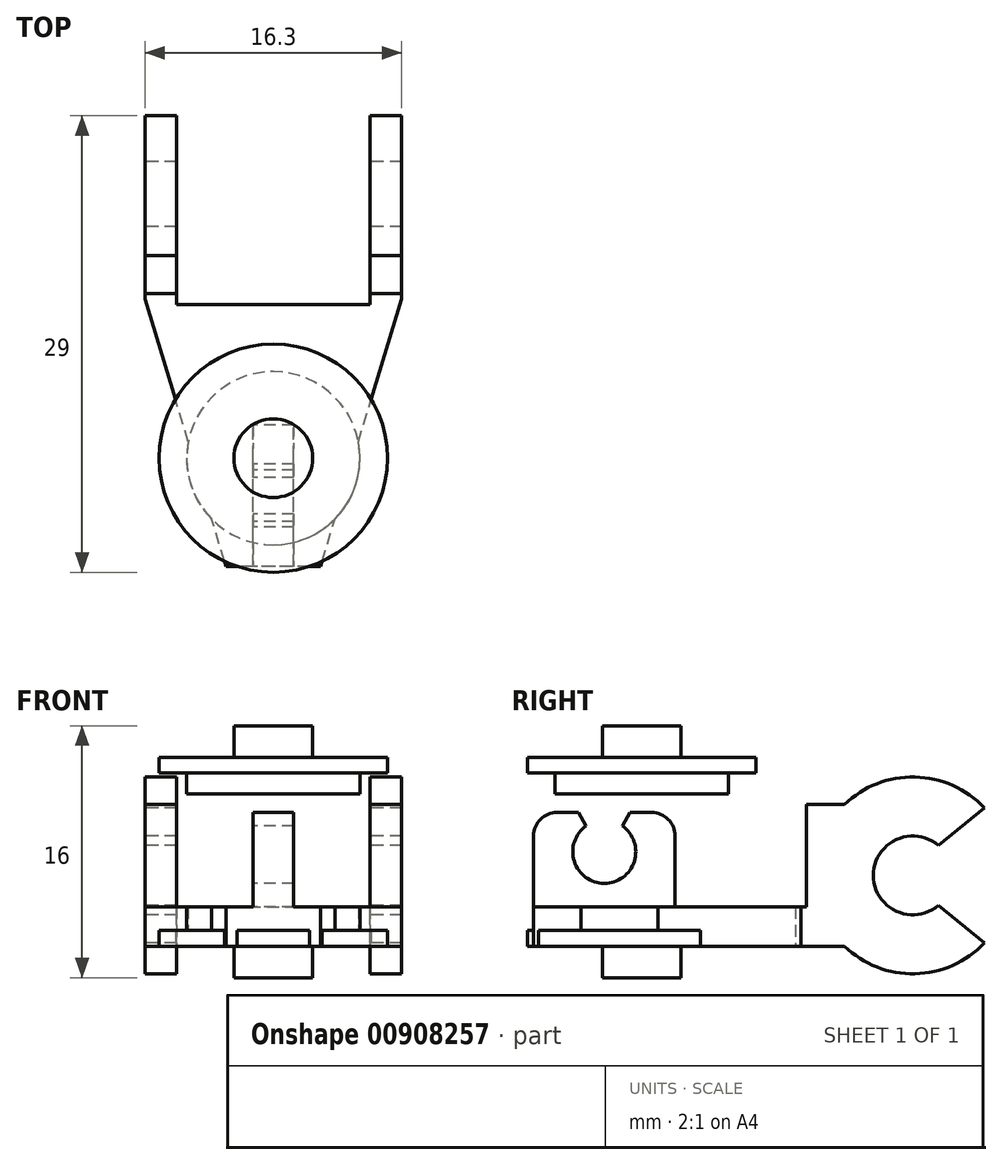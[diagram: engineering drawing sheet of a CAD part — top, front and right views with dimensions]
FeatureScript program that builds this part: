
annotation { "Feature Type Name" : "Feature", "Feature Type Description" : "" }
export const myFeature = defineFeature(function(context is Context, id is Id, definition is map)
    precondition{}
    {
        {
            var Q0;
            Q0=qCreatedBy(makeId("Top.planeOp"),FACE);
            var sketch = newSketch(context, id + "F0", { "sketchPlane" : qUnion([Q0])});
            skCircle(sketch, "E0", {"center": v(0, 0) * mm, "radius": 7.25 * mm});
            skSolve(sketch);
        }
        {
            var Q0;
            Q0 = qSketchRegion(id + "F0", true);
            extrude(context, id + "F1", {"entities" : qUnion([Q0]), "depth" : 1 * mm, "offsetDistance" : 25 * mm});
        }
        {
            var Q0;
            Q0=makeQuery(id+"F1.opExtrude","CAP_FACE",FACE,{"disambiguationData":[OSD([sQuery(id+"F0.wireOp",EDGE,"E0")])],"isStart":false});
            var sketch = newSketch(context, id + "F2", { "sketchPlane" : qUnion([Q0])});
            skCircle(sketch, "E1", {"center": v(0, 0) * mm, "radius": 5.5 * mm});
            skSolve(sketch);
        }
        {
            var Q0;
            Q0 = qSketchRegion(id + "F2", true);
            extrude(context, id + "F3", {"entities" : qUnion([Q0]), "operationType" : NewBodyOperationType.ADD, "depth" : 5 * mm, "offsetDistance" : 25 * mm});
        }
        {
            var Q0;
            Q0=makeQuery(id+"F1.opExtrude","CAP_FACE",FACE,{"disambiguationData":[OSD([sQuery(id+"F0.wireOp",EDGE,"E0")])],"isStart":true});
            var sketch = newSketch(context, id + "F4", { "sketchPlane" : qUnion([Q0])});
            skCircle(sketch, "E2", {"center": v(0, 0) * mm, "radius": 2.5 * mm});
            skSolve(sketch);
        }
        {
            var Q0;
            Q0 = qSketchRegion(id + "F4", true);
            extrude(context, id + "F5", {"entities" : qUnion([Q0]), "operationType" : NewBodyOperationType.ADD, "depth" : 2 * mm, "offsetDistance" : 25 * mm});
        }
        {
            var Q0;
            Q0=makeQuery(id+"F1.opExtrude","SWEPT_BODY",BODY,{"disambiguationData":[OSD([sQuery(id+"F0.wireOp",EDGE,"E0")])]});
            var Q1;
            Q1=makeQuery(id+"F3.opExtrude","CAP_FACE",FACE,{"disambiguationData":[OSD([sQuery(id+"F2.wireOp",EDGE,"E1")])],"isStart":false});
            mirror(context, id + "F6", {"operationType" : NewBodyOperationType.ADD, "entities" : qUnion([Q0]), "mirrorPlane" : qUnion([Q1])});
        }
        {
            var Q0;
            Q0=qCreatedBy(makeId("Top.planeOp"),FACE);
            var sketch = newSketch(context, id + "F7", { "sketchPlane" : qUnion([Q0])});
            skLineSegment(sketch, "E3", {"start": v(0, 13.12) * mm, "end": v(8.15, 13.12) * mm});
            skLineSegment(sketch, "E4", {"start": v(8.15, 13.12) * mm, "end": v(8.15, 10.12) * mm});
            skLineSegment(sketch, "E5", {"start": v(0, -6.88) * mm, "end": v(3, -6.88) * mm});
            skLineSegment(sketch, "E6", {"start": v(3, -6.88) * mm, "end": v(8.15, 10.12) * mm});
            skLineSegment(sketch, "E7.MirrorCS", {"start": v(-8.15, 13.12) * mm, "end": v(-8.15, 10.12) * mm});
            skLineSegment(sketch, "E8.MirrorCS", {"start": v(0, -6.88) * mm, "end": v(-3, -6.88) * mm});
            skLineSegment(sketch, "E9.MirrorCS", {"start": v(0, 13.12) * mm, "end": v(-8.15, 13.12) * mm});
            skLineSegment(sketch, "E10.MirrorCS", {"start": v(-3, -6.88) * mm, "end": v(-8.15, 10.12) * mm});
            skSolve(sketch);
        }
        {
            var Q0;
            Q0=makeQuery(id+"F7.imprint","IMPRINT",FACE,{"disambiguationData":[TD([[makeQuery(id+"F7.imprint","IMPRINT",EDGE,{"derivedFrom":sQuery(id+"F7.wireOp",EDGE,"E3")}),-1.0]])]});
            extrude(context, id + "F8", {"entities" : qUnion([Q0]), "depth" : 9 * mm, "offsetDistance" : 25 * mm});
        }
        {
            var Q0;
            Q0=qCreatedBy(makeId("Right.planeOp"),FACE);
            var sketch = newSketch(context, id + "F9", { "sketchPlane" : qUnion([Q0])});
            skArc(sketch, "E11", {"start": v(21.75, 8.8) * mm, "mid": v(10.96, 4.5) * mm, "end": v(21.75, 0.2) * mm});
            skArc(sketch, "E12", {"start": v(18.84, 6.4) * mm, "mid": v(14.71, 4.5) * mm, "end": v(18.84, 2.6) * mm});
            skLineSegment(sketch, "E13", {"start": v(21.75, 8.8) * mm, "end": v(18.84, 6.4) * mm});
            skLineSegment(sketch, "E14", {"start": v(21.27, 4.5) * mm, "end": v(10, 4.5) * mm, "construction": true});
            skLineSegment(sketch, "E15.MirrorCS", {"start": v(21.75, 0.2) * mm, "end": v(18.84, 2.6) * mm});
            skSolve(sketch);
        }
        {
            var Q0;
            Q0 = qSketchRegion(id + "F9", true);
            extrude(context, id + "F10", {"entities" : qUnion([Q0]), "operationType" : NewBodyOperationType.ADD, "depth" : 8.15 * mm, "offsetDistance" : 25 * mm, "hasSecondDirection" : true, "secondDirectionOppositeDirection" : true, "secondDirectionDepth" : 8.15 * mm});
        }
        {
            var Q0;
            Q0=qCreatedBy(makeId("Top.planeOp"),FACE);
            var sketch = newSketch(context, id + "F11", { "sketchPlane" : qUnion([Q0])});
            skLineSegment(sketch, "E16.bottom", {"start": v(-6.15, 23.07) * mm, "end": v(6.15, 23.07) * mm});
            skLineSegment(sketch, "E16.top", {"start": v(-6.15, 9.75) * mm, "end": v(6.15, 9.75) * mm});
            skLineSegment(sketch, "E16.left", {"start": v(-6.15, 23.07) * mm, "end": v(-6.15, 9.75) * mm});
            skLineSegment(sketch, "E16.right", {"start": v(6.15, 23.07) * mm, "end": v(6.15, 9.75) * mm});
            skSolve(sketch);
        }
        {
            var Q0;
            Q0 = qSketchRegion(id + "F11", true);
            extrude(context, id + "F12", {"entities" : qUnion([Q0]), "operationType" : NewBodyOperationType.REMOVE, "depth" : 25 * mm, "offsetDistance" : 25 * mm, "hasSecondDirection" : true, "secondDirectionOppositeDirection" : true, "secondDirectionDepth" : 25 * mm});
        }
        {
            var Q0;
            Q0=qCreatedBy(makeId("Right.planeOp"),FACE);
            var sketch = newSketch(context, id + "F13", { "sketchPlane" : qUnion([Q0])});
            skLineSegment(sketch, "E17.bottom", {"start": v(10.45, 9.67) * mm, "end": v(-8.04, 9.67) * mm});
            skLineSegment(sketch, "E17.top", {"start": v(10.45, 2.5) * mm, "end": v(-8.04, 2.5) * mm});
            skLineSegment(sketch, "E17.left", {"start": v(10.45, 9.67) * mm, "end": v(10.45, 2.5) * mm});
            skLineSegment(sketch, "E17.right", {"start": v(-8.04, 9.67) * mm, "end": v(-8.04, 2.5) * mm});
            skSolve(sketch);
        }
        {
            var Q0;
            Q0 = qSketchRegion(id + "F13", true);
            extrude(context, id + "F14", {"entities" : qUnion([Q0]), "operationType" : NewBodyOperationType.REMOVE, "oppositeDirection" : true, "depth" : 25 * mm, "offsetDistance" : 25 * mm, "hasSecondDirection" : true, "secondDirectionOppositeDirection" : false, "secondDirectionDepth" : 25 * mm});
        }
        {
            var Q0;
            Q0=qCreatedBy(makeId("Right.planeOp"),FACE);
            var sketch = newSketch(context, id + "F15", { "sketchPlane" : qUnion([Q0])});
            skLineSegment(sketch, "E18.bottom", {"start": v(-6.88, 2.5) * mm, "end": v(2.12, 2.5) * mm});
            skLineSegment(sketch, "E18.top", {"start": v(-6.88, 8.5) * mm, "end": v(-4, 8.5) * mm});
            skLineSegment(sketch, "E18.left", {"start": v(-6.88, 2.5) * mm, "end": v(-6.88, 8.5) * mm});
            skLineSegment(sketch, "E18.right", {"start": v(2.12, 2.5) * mm, "end": v(2.12, 8.5) * mm});
            skArc(sketch, "E19", {"start": v(-3.53, 7.63) * mm, "mid": v(-2.38, 4) * mm, "end": v(-1.22, 7.63) * mm});
            skLineSegment(sketch, "E20", {"start": v(-2.38, 6) * mm, "end": v(-2.38, 9.33) * mm, "construction": true});
            skLineSegment(sketch, "E21", {"start": v(-1.22, 7.63) * mm, "end": v(-0.75, 8.5) * mm});
            skLineSegment(sketch, "E22.MirrorCS", {"start": v(-3.53, 7.63) * mm, "end": v(-4, 8.5) * mm});
            skLineSegment(sketch, "E23.trimOffspring", {"start": v(-0.75, 8.5) * mm, "end": v(2.12, 8.5) * mm});
            skSolve(sketch);
        }
        {
            var Q0;
            Q0 = qSketchRegion(id + "F15", true);
            extrude(context, id + "F16", {"entities" : qUnion([Q0]), "operationType" : NewBodyOperationType.ADD, "depth" : 1.3 * mm, "offsetDistance" : 25 * mm, "hasSecondDirection" : true, "secondDirectionOppositeDirection" : true, "secondDirectionDepth" : 1.3 * mm});
        }
        {
            var Q0;
            Q0=makeQuery(id+"F16.opExtrude","SWEPT_EDGE",EDGE,{"disambiguationData":[OSD([sQuery(id+"F15.wireOp",EDGE,"E18.top"),sQuery(id+"F15.wireOp",EDGE,"E18.left")])]});
            var Q1;
            Q1=makeQuery(id+"F16.opExtrude","SWEPT_EDGE",EDGE,{"disambiguationData":[OSD([sQuery(id+"F15.wireOp",EDGE,"E18.right"),sQuery(id+"F15.wireOp",EDGE,"E23.trimOffspring")])]});
            fillet(context, id + "F17", {"entities" : qUnion([Q0, Q1]), "radius" : 1.5 * mm, "tangentPropagation" : true, "allowEdgeOverflow" : false});
        }
    });
